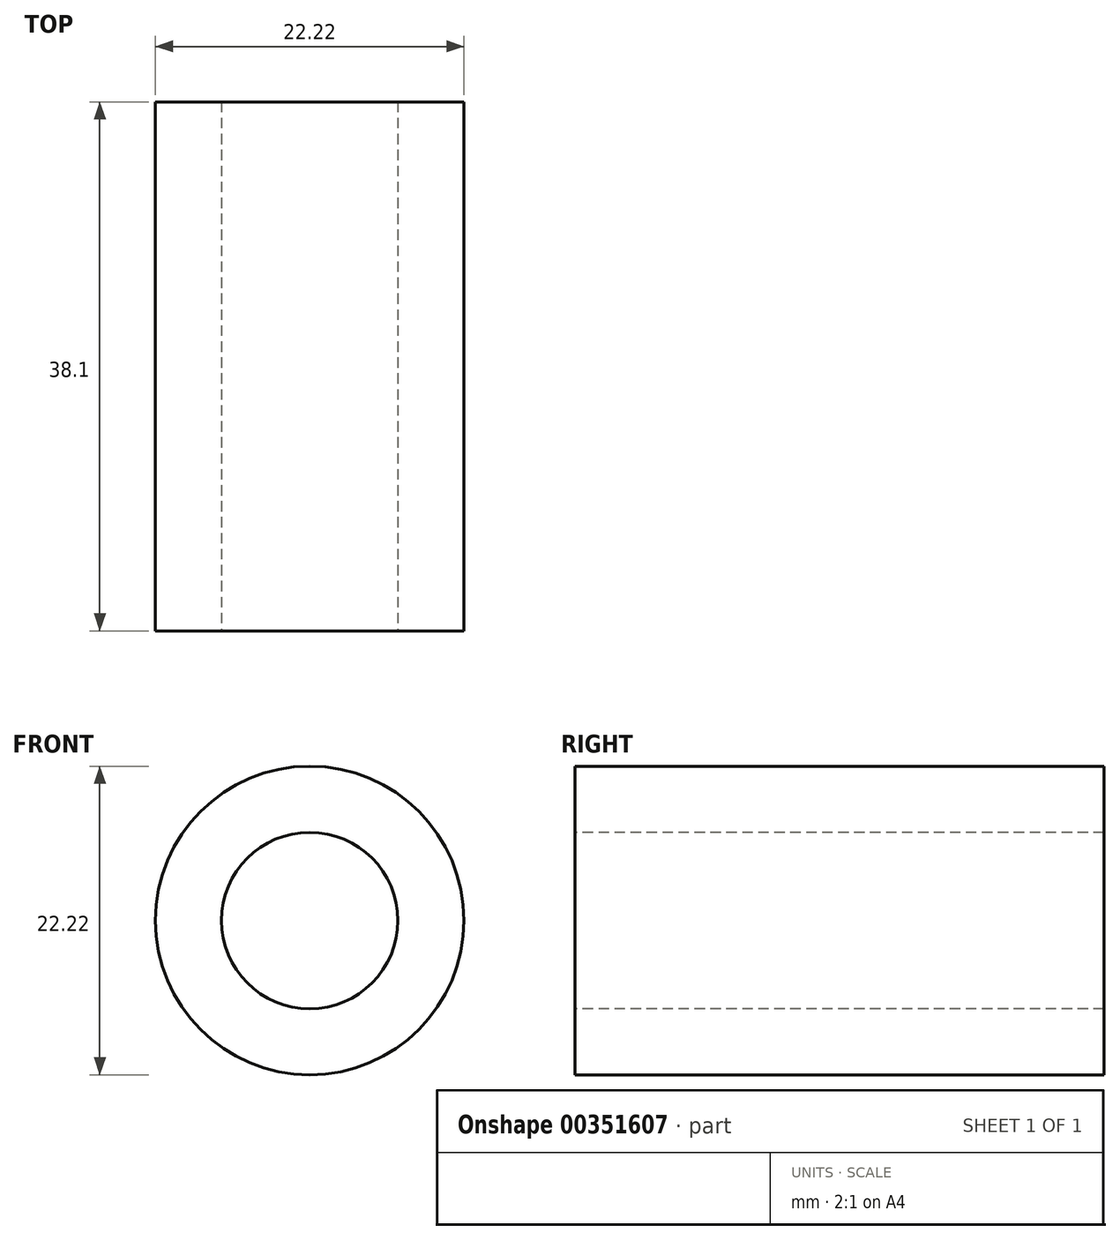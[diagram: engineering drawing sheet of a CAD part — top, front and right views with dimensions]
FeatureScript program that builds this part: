
annotation { "Feature Type Name" : "Feature", "Feature Type Description" : "" }
export const myFeature = defineFeature(function(context is Context, id is Id, definition is map)
    precondition{}
    {
        {
            var Q0;
            Q0=qCreatedBy(makeId("Front.planeOp"),FACE);
            var sketch = newSketch(context, id + "F0", { "sketchPlane" : qUnion([Q0])});
            skCircle(sketch, "E0", {"center": v(0, 0) * mm, "radius": 11.11 * mm});
            skSolve(sketch);
        }
        {
            var Q0;
            Q0=makeQuery(id+"F0.imprint","IMPRINT",FACE,{"disambiguationData":[TD([[makeQuery(id+"F0.imprint","IMPRINT",EDGE,{"derivedFrom":sQuery(id+"F0.wireOp",EDGE,"E0")}),1.0]])]});
            extrude(context, id + "F1", {"entities" : qUnion([Q0]), "depth" : 38.1 * mm, "symmetric" : true});
        }
        {
            var Q0;
            Q0=qCreatedBy(makeId("Front.planeOp"),FACE);
            var sketch = newSketch(context, id + "F2", { "sketchPlane" : qUnion([Q0])});
            skCircle(sketch, "E1", {"center": v(0, 0) * mm, "radius": 6.35 * mm});
            skSolve(sketch);
        }
        {
            var Q0;
            Q0 = qSketchRegion(id + "F2", true);
            extrude(context, id + "F3", {"entities" : qUnion([Q0]), "operationType" : NewBodyOperationType.REMOVE, "oppositeDirection" : true, "depth" : 38.1 * mm, "symmetric" : true});
        }
    });
